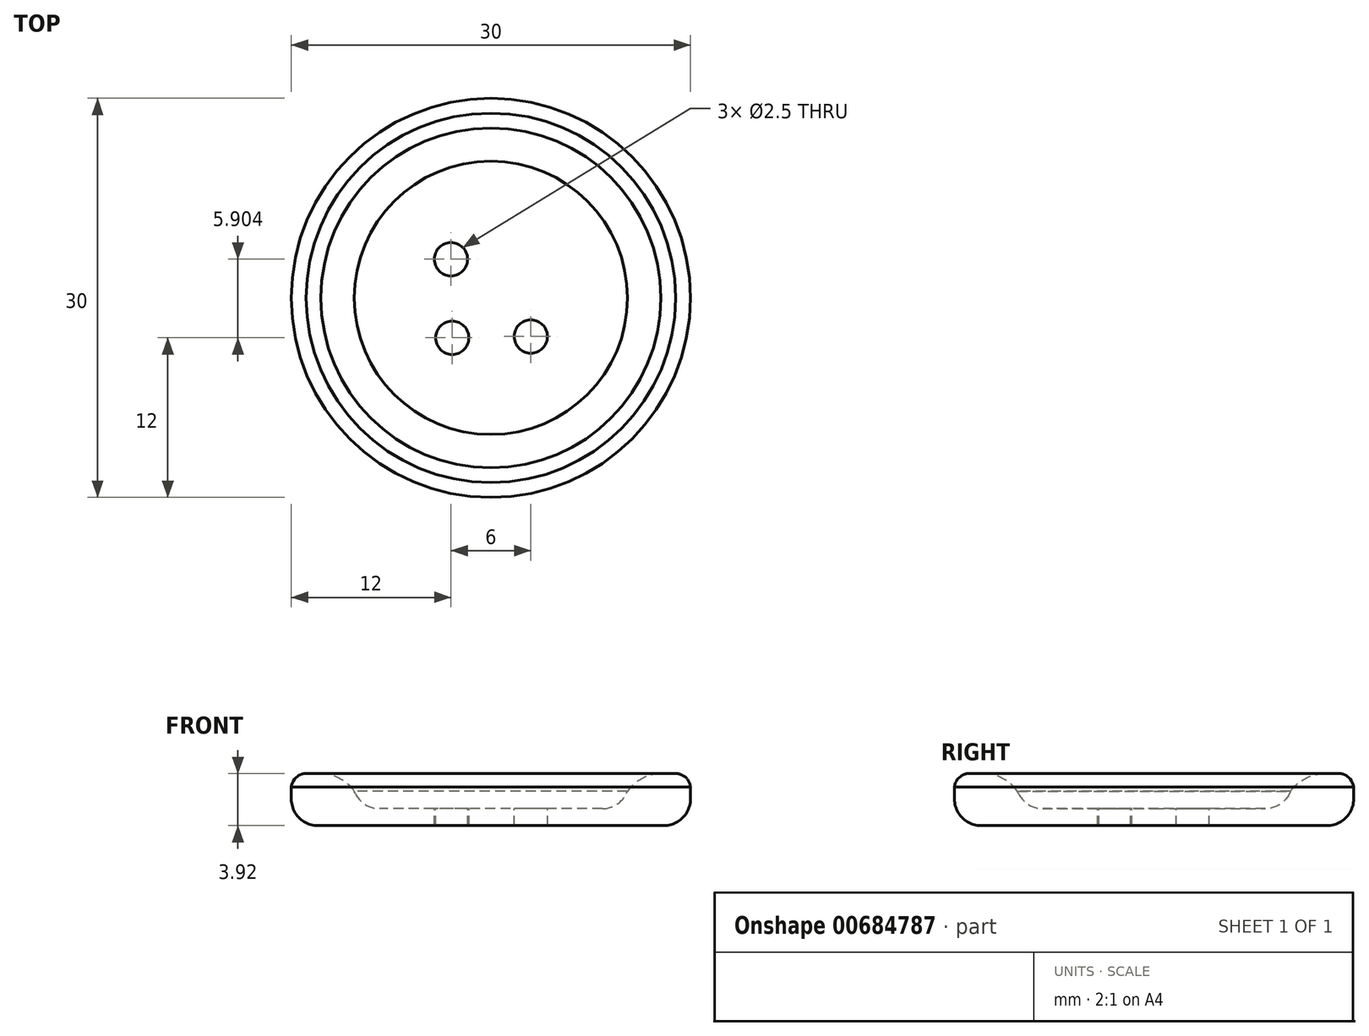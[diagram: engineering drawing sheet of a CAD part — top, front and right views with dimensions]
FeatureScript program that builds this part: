
annotation { "Feature Type Name" : "Feature", "Feature Type Description" : "" }
export const myFeature = defineFeature(function(context is Context, id is Id, definition is map)
    precondition{}
    {
        {
            var Q0;
            Q0=qCreatedBy(makeId("Front.planeOp"),FACE);
            var sketch = newSketch(context, id + "F0", { "sketchPlane" : qUnion([Q0])});
            skLineSegment(sketch, "E0", {"start": v(0, 0) * mm, "end": v(13, 0) * mm});
            skLineSegment(sketch, "E1", {"start": v(15, 2) * mm, "end": v(15, 2.9) * mm});
            skLineSegment(sketch, "E2", {"start": v(13.89, 3.92) * mm, "end": v(12.77, 3.92) * mm});
            skLineSegment(sketch, "E3", {"start": v(10.27, 2.6) * mm, "end": v(10.2, 2.44) * mm});
            skLineSegment(sketch, "E4", {"start": v(8.38, 1.28) * mm, "end": v(0, 1.28) * mm});
            skLineSegment(sketch, "E5", {"start": v(0, 1.28) * mm, "end": v(0, 0) * mm});
            skArc(sketch, "E6", {"start": v(12.77, 3.92) * mm, "mid": v(11.37, 3.55) * mm, "end": v(10.27, 2.6) * mm});
            skPoint(sketch, "E7.orphan", {"position": v(10.88, 3.92) * mm});
            skArc(sketch, "E8", {"start": v(15, 2.9) * mm, "mid": v(14.64, 3.62) * mm, "end": v(13.89, 3.92) * mm});
            skPoint(sketch, "E9.orphan", {"position": v(15, 3.92) * mm});
            skPoint(sketch, "E10.visualSharp", {"position": v(15, 0) * mm});
            skArc(sketch, "E10.filletArc", {"start": v(13, 0) * mm, "mid": v(14.41, 0.59) * mm, "end": v(15, 2) * mm});
            skPoint(sketch, "E11.visualSharp", {"position": v(9.66, 1.28) * mm});
            skArc(sketch, "E11.filletArc", {"start": v(8.38, 1.28) * mm, "mid": v(9.46, 1.6) * mm, "end": v(10.2, 2.44) * mm});
            skSolve(sketch);
        }
        {
            var Q0;
            Q0=makeQuery(id+"F0.imprint","IMPRINT",FACE,{"disambiguationData":[TD([[makeQuery(id+"F0.imprint","IMPRINT",EDGE,{"derivedFrom":sQuery(id+"F0.wireOp",EDGE,"E0")}),1.0]])]});
            var Q1;
            Q1 = qSketchRegion(id + "F2", true);
            var Q2;
            Q2=sQuery(id+"F0.wireOp",EDGE,"E5");
            revolve(context, id + "F1", {"entities" : qUnion([Q0, Q1]), "axis" : qUnion([Q2]), "revolveType" : RevolveType.FULL});
        }
        {
            var Q0;
            Q0=makeQuery(id+"F1.opRevolve","SWEPT_FACE",FACE,{"disambiguationData":[OSD([sQuery(id+"F0.wireOp",EDGE,"E4")])]});
            var sketch = newSketch(context, id + "F2", { "sketchPlane" : qUnion([Q0])});
            skCircle(sketch, "E12", {"center": v(2.9, 3) * mm, "radius": 1.25 * mm});
            skCircle(sketch, "E13.1.0", {"center": v(3, -2.9) * mm, "radius": 1.25 * mm});
            skCircle(sketch, "E13.2.0", {"center": v(-2.9, -3) * mm, "radius": 1.25 * mm});
            skPoint(sketch, "E13.center", {"position": v(0, 0) * mm});
            skLineSegment(sketch, "E13.anchor1", {"start": v(0, 0) * mm, "end": v(2.9, 3) * mm, "construction": true});
            skLineSegment(sketch, "E13.anchor2", {"start": v(0, 0) * mm, "end": v(-2.9, -3) * mm, "construction": true});
            skCircle(sketch, "E14.1.0", {"center": v(-3, 2.9) * mm, "radius": 1.25 * mm});
            skSolve(sketch);
        }
        {
            var Q0;
            Q0=makeQuery(id+"F2.imprint","IMPRINT",FACE,{"disambiguationData":[TD([[makeQuery(id+"F2.imprint","IMPRINT",EDGE,{"derivedFrom":sQuery(id+"F2.wireOp",EDGE,"E13.1.0")}),1.0]])]});
            var Q1;
            Q1=makeQuery(id+"F2.imprint","IMPRINT",FACE,{"disambiguationData":[TD([[makeQuery(id+"F2.imprint","IMPRINT",EDGE,{"derivedFrom":sQuery(id+"F2.wireOp",EDGE,"E12")}),1.0]])]});
            var Q2;
            Q2=makeQuery(id+"F2.imprint","IMPRINT",FACE,{"disambiguationData":[TD([[makeQuery(id+"F2.imprint","IMPRINT",EDGE,{"derivedFrom":sQuery(id+"F2.wireOp",EDGE,"E14.1.0")}),1.0]])]});
            var Q3;
            Q3=makeQuery(id+"F2.imprint","IMPRINT",FACE,{"disambiguationData":[TD([[makeQuery(id+"F2.imprint","IMPRINT",EDGE,{"derivedFrom":sQuery(id+"F2.wireOp",EDGE,"E13.2.0")}),1.0]])]});
            var Q4;
            Q4=sQuery(id+"F2.wireOp",EDGE,"E12");
            var Q5;
            Q5=sQuery(id+"F2.wireOp",EDGE,"E14.1.0");
            var Q6;
            Q6=sQuery(id+"F2.wireOp",EDGE,"E13.2.0");
            var Q7;
            Q7=sQuery(id+"F2.wireOp",EDGE,"E13.1.0");
            extrude(context, id + "F3", {"entities" : qUnion([Q0, Q1, Q2, Q3]), "operationType" : NewBodyOperationType.REMOVE, "surfaceEntities" : qUnion([Q4, Q5, Q6, Q7]), "oppositeDirection" : true, "depth" : 5.1 * mm, "offsetDistance" : 25 * mm});
        }
    });
